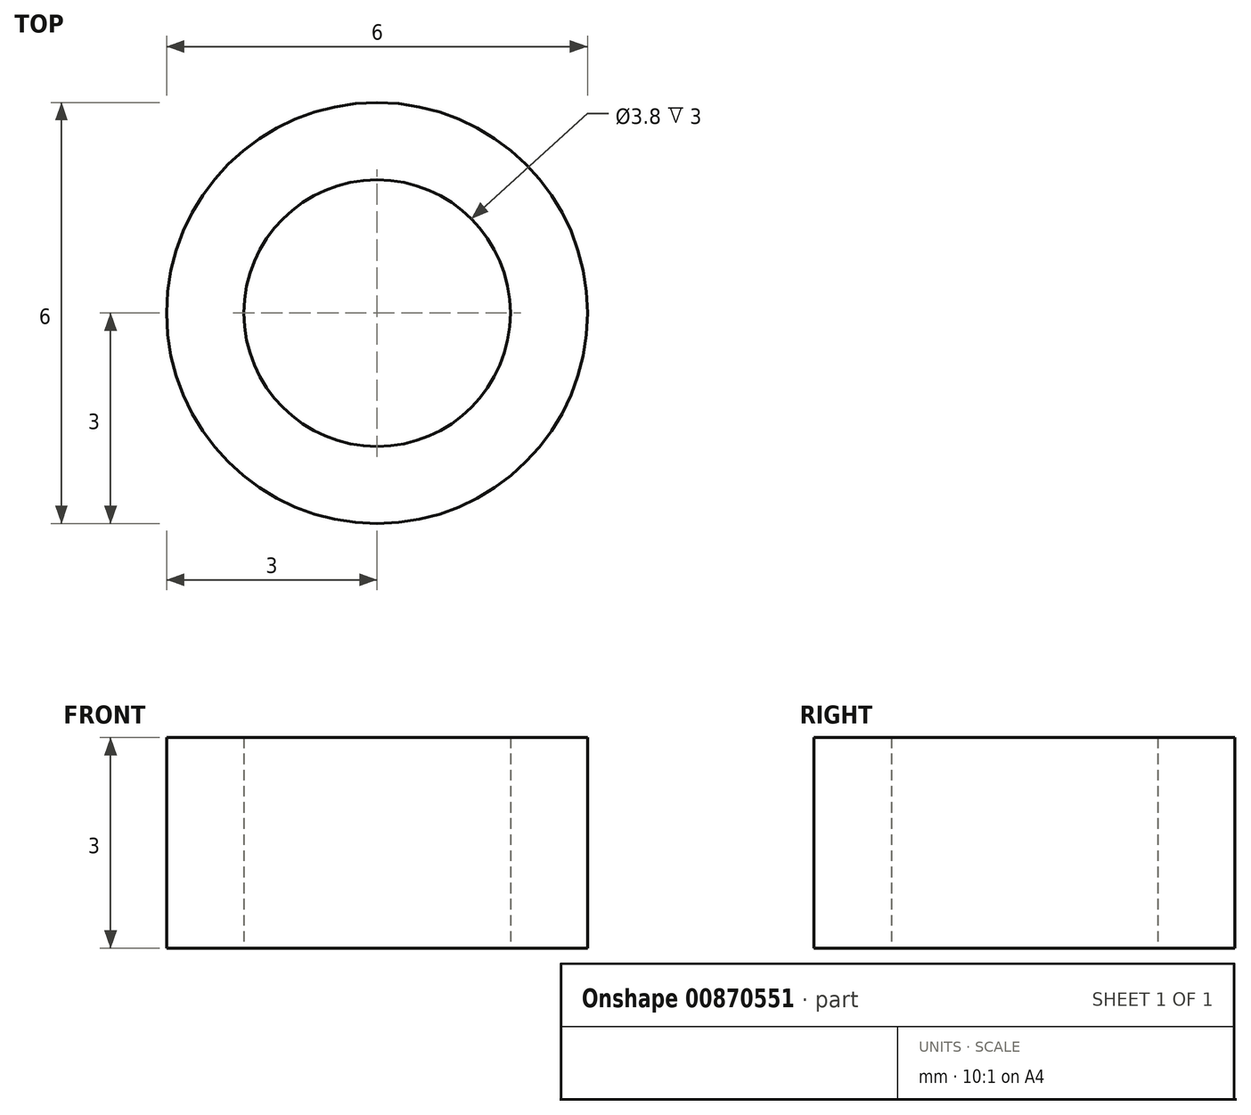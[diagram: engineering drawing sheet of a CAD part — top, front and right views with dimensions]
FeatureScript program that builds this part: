
annotation { "Feature Type Name" : "Feature", "Feature Type Description" : "" }
export const myFeature = defineFeature(function(context is Context, id is Id, definition is map)
    precondition{}
    {
        {
            var Q0;
            Q0=qCreatedBy(makeId("Top.planeOp"),FACE);
            var sketch = newSketch(context, id + "F0", { "sketchPlane" : qUnion([Q0])});
            skCircle(sketch, "E0", {"center": v(0, 0) * mm, "radius": 3 * mm});
            skCircle(sketch, "E1", {"center": v(0, 0) * mm, "radius": 1.9 * mm});
            skSolve(sketch);
        }
        {
            var Q0;
            Q0=makeQuery(id+"F0.imprint","IMPRINT",FACE,{"disambiguationData":[TD([[makeQuery(id+"F0.imprint","IMPRINT",EDGE,{"derivedFrom":sQuery(id+"F0.wireOp",EDGE,"E0")}),1.0]])]});
            extrude(context, id + "F1", {"entities" : qUnion([Q0]), "depth" : 3 * mm, "offsetDistance" : 25 * mm});
        }
    });
